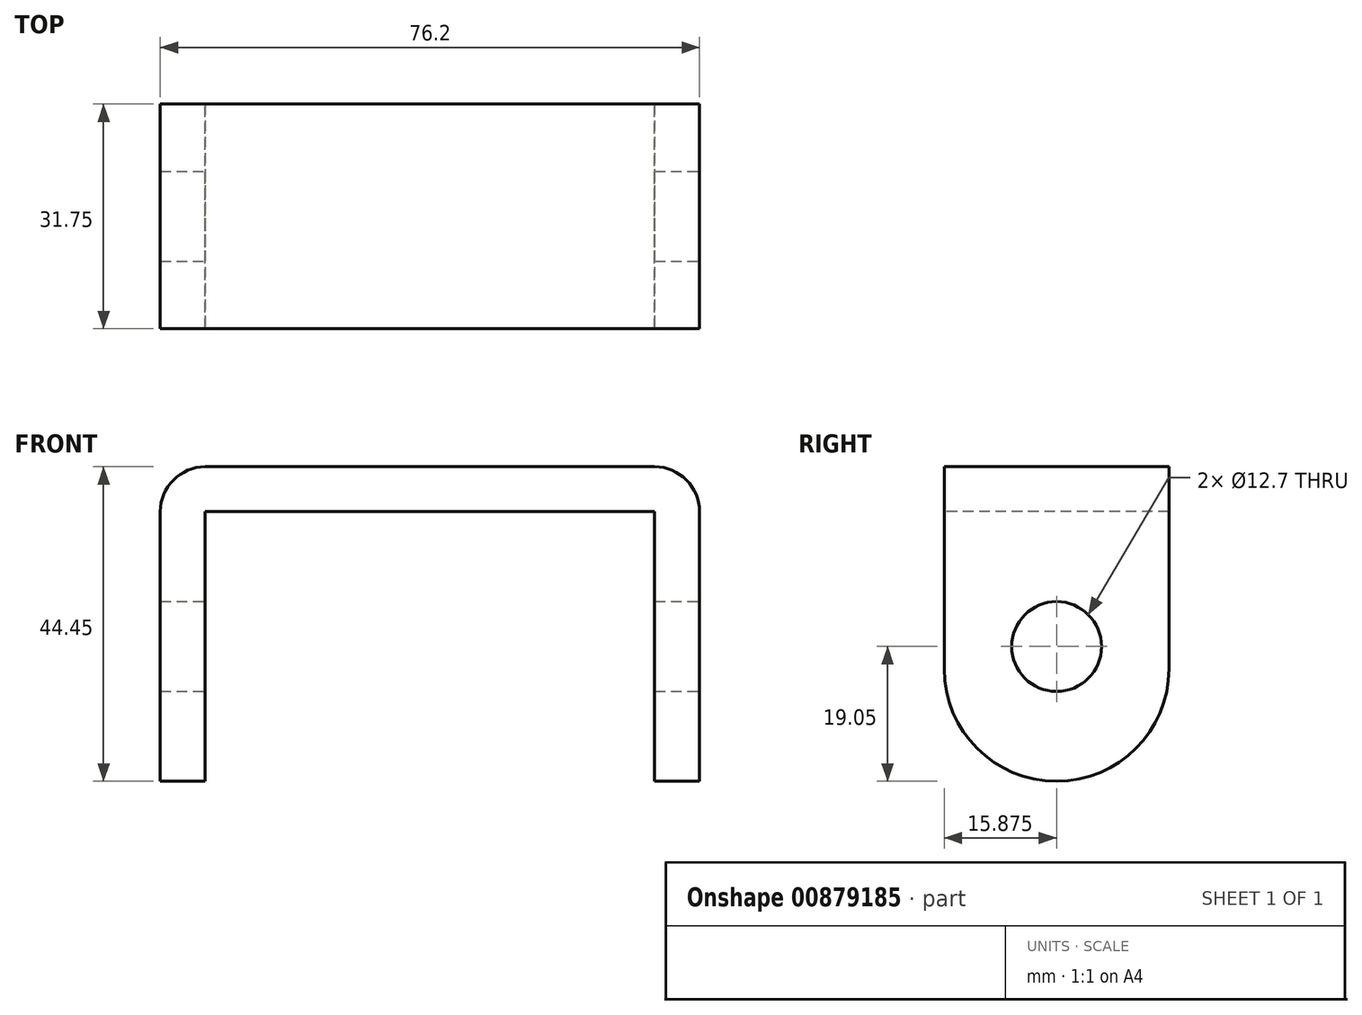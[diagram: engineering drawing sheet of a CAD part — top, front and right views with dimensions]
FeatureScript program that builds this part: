
annotation { "Feature Type Name" : "Feature", "Feature Type Description" : "" }
export const myFeature = defineFeature(function(context is Context, id is Id, definition is map)
    precondition{}
    {
        {
            var Q0;
            Q0=qCreatedBy(makeId("Front.planeOp"),FACE);
            var sketch = newSketch(context, id + "F0", { "sketchPlane" : qUnion([Q0])});
            skLineSegment(sketch, "E0.bottom", {"start": v(0, 0) * mm, "end": v(-76.2, 0) * mm});
            skLineSegment(sketch, "E0.top", {"start": v(0, 6.35) * mm, "end": v(-76.2, 6.35) * mm});
            skLineSegment(sketch, "E0.left", {"start": v(0, 0) * mm, "end": v(0, 6.35) * mm});
            skLineSegment(sketch, "E0.right", {"start": v(-76.2, 0) * mm, "end": v(-76.2, 6.35) * mm});
            skLineSegment(sketch, "E1.bottom", {"start": v(-76.2, 0) * mm, "end": v(-69.85, 0) * mm});
            skLineSegment(sketch, "E1.top", {"start": v(-76.2, -38.1) * mm, "end": v(-69.85, -38.1) * mm});
            skLineSegment(sketch, "E1.left", {"start": v(-76.2, 0) * mm, "end": v(-76.2, -38.1) * mm});
            skLineSegment(sketch, "E1.right", {"start": v(-69.85, 0) * mm, "end": v(-69.85, -38.1) * mm});
            skLineSegment(sketch, "E2.bottom", {"start": v(0, 0) * mm, "end": v(-6.35, 0) * mm});
            skLineSegment(sketch, "E2.top", {"start": v(0, -38.1) * mm, "end": v(-6.35, -38.1) * mm});
            skLineSegment(sketch, "E2.left", {"start": v(0, 0) * mm, "end": v(0, -38.1) * mm});
            skLineSegment(sketch, "E2.right", {"start": v(-6.35, 0) * mm, "end": v(-6.35, -38.1) * mm});
            skSolve(sketch);
        }
        {
            var Q0;
            Q0=qSketchRegion(id+"F0",true);
            extrude(context, id + "F1", {"entities" : qUnion([Q0]), "depth" : 31.75 * mm, "offsetDistance" : 25.4 * mm});
        }
        {
            var Q0;
            Q0=makeQuery(id+"F1.opExtrude","SWEPT_FACE",FACE,{"disambiguationData":[OSD([sQuery(id+"F0.wireOp",EDGE,"E0.left"),sQuery(id+"F0.wireOp",EDGE,"E2.left")])]});
            var sketch = newSketch(context, id + "F2", { "sketchPlane" : qUnion([Q0])});
            skCircle(sketch, "E3", {"center": v(-15.88, -19.05) * mm, "radius": 6.35 * mm});
            skSolve(sketch);
        }
        {
            var Q0;
            Q0=qSketchRegion(id+"F2",true);
            extrude(context, id + "F3", {"entities" : qUnion([Q0]), "operationType" : NewBodyOperationType.REMOVE, "oppositeDirection" : true, "depth" : 127 * mm, "offsetDistance" : 25.4 * mm});
        }
        {
            var Q0;
            Q0=makeQuery(id+"F1.opExtrude","SWEPT_FACE",FACE,{"disambiguationData":[OSD([sQuery(id+"F0.wireOp",EDGE,"E0.left"),sQuery(id+"F0.wireOp",EDGE,"E2.left")])]});
            var sketch = newSketch(context, id + "F4", { "sketchPlane" : qUnion([Q0])});
            skLineSegment(sketch, "E4.bottom", {"start": v(-15.88, -38.1) * mm, "end": v(-15.87, -38.1) * mm});
            skLineSegment(sketch, "E4.top", {"start": v(-31.75, 6.35) * mm, "end": v(0, 6.35) * mm});
            skLineSegment(sketch, "E4.left", {"start": v(-31.75, -22.23) * mm, "end": v(-31.75, 6.35) * mm});
            skLineSegment(sketch, "E4.right", {"start": v(0, -22.22) * mm, "end": v(0, 6.35) * mm});
            skPoint(sketch, "E5.visualSharp", {"position": v(-31.75, -38.1) * mm});
            skArc(sketch, "E5.filletArc", {"start": v(-31.75, -22.23) * mm, "mid": v(-27.1, -33.45) * mm, "end": v(-15.88, -38.1) * mm});
            skPoint(sketch, "E6.visualSharp", {"position": v(0, -38.1) * mm});
            skArc(sketch, "E6.filletArc", {"start": v(-15.87, -38.1) * mm, "mid": v(-4.65, -33.45) * mm, "end": v(0, -22.22) * mm});
            skSolve(sketch);
        }
        {
            var Q0;
            {var subQ0=sQuery(id+"F4.wireOp",EDGE,"E5.filletArc");Q0=makeQuery(id+"F4.imprint","IMPRINT",FACE,{"disambiguationData":[TD([[makeQuery(id+"F4.imprint","IMPRINT",EDGE,{"derivedFrom":subQ0}),-1.0]])]});}
            var Q1;
            {var subQ0=sQuery(id+"F4.wireOp",EDGE,"E6.filletArc");Q1=makeQuery(id+"F4.imprint","IMPRINT",FACE,{"disambiguationData":[TD([[makeQuery(id+"F4.imprint","IMPRINT",EDGE,{"derivedFrom":subQ0}),-1.0]])]});}
            extrude(context, id + "F5", {"entities" : qUnion([Q0, Q1]), "operationType" : NewBodyOperationType.REMOVE, "oppositeDirection" : true, "depth" : 127 * mm, "offsetDistance" : 25.4 * mm});
        }
        {
            var Q0;
            Q0=makeQuery(id+"F1.opExtrude","CAP_FACE",FACE,{"disambiguationData":[OSD([sQuery(id+"F0.wireOp",EDGE,"E0.bottom"),sQuery(id+"F0.wireOp",EDGE,"E0.top"),sQuery(id+"F0.wireOp",EDGE,"E0.left"),sQuery(id+"F0.wireOp",EDGE,"E0.right"),sQuery(id+"F0.wireOp",EDGE,"E1.top"),sQuery(id+"F0.wireOp",EDGE,"E1.left"),sQuery(id+"F0.wireOp",EDGE,"E1.right"),sQuery(id+"F0.wireOp",EDGE,"E2.top"),sQuery(id+"F0.wireOp",EDGE,"E2.left"),sQuery(id+"F0.wireOp",EDGE,"E2.right")])],"isStart":false});
            var sketch = newSketch(context, id + "F6", { "sketchPlane" : qUnion([Q0])});
            skLineSegment(sketch, "E7.bottom", {"start": v(-69.85, 6.35) * mm, "end": v(-6.35, 6.35) * mm});
            skLineSegment(sketch, "E7.top", {"start": v(-63.5, 0) * mm, "end": v(-12.7, 0) * mm});
            skLineSegment(sketch, "E7.left", {"start": v(-76.2, 0) * mm, "end": v(-76.2, 0) * mm});
            skLineSegment(sketch, "E7.right", {"start": v(0, 0) * mm, "end": v(0, 0) * mm});
            skLineSegment(sketch, "E8.bottom", {"start": v(0, 0) * mm, "end": v(-6.35, 0) * mm});
            skLineSegment(sketch, "E8.top", {"start": v(0, -22.23) * mm, "end": v(-6.35, -22.23) * mm});
            skLineSegment(sketch, "E8.left", {"start": v(0, 0) * mm, "end": v(0, -22.23) * mm});
            skLineSegment(sketch, "E8.right", {"start": v(-6.35, -6.35) * mm, "end": v(-6.35, -22.23) * mm});
            skLineSegment(sketch, "E9.bottom", {"start": v(-69.85, -22.23) * mm, "end": v(-76.2, -22.23) * mm});
            skLineSegment(sketch, "E9.top", {"start": v(-69.85, 0) * mm, "end": v(-76.2, 0) * mm});
            skLineSegment(sketch, "E9.left", {"start": v(-69.85, -22.23) * mm, "end": v(-69.85, -6.35) * mm});
            skLineSegment(sketch, "E9.right", {"start": v(-76.2, -22.23) * mm, "end": v(-76.2, 0) * mm});
            skPoint(sketch, "E10.visualSharp", {"position": v(-76.2, 6.35) * mm});
            skArc(sketch, "E10.filletArc", {"start": v(-69.85, 6.35) * mm, "mid": v(-74.34, 4.5) * mm, "end": v(-76.2, 0) * mm});
            skArc(sketch, "E11.filletArc", {"start": v(-63.5, 0) * mm, "mid": v(-68, -1.86) * mm, "end": v(-69.85, -6.35) * mm});
            skArc(sketch, "E12.filletArc", {"start": v(-6.35, -6.35) * mm, "mid": v(-8.2, -1.86) * mm, "end": v(-12.7, 0) * mm});
            skPoint(sketch, "E13.visualSharp", {"position": v(0, 6.35) * mm});
            skArc(sketch, "E13.filletArc", {"start": v(0, 0) * mm, "mid": v(-1.86, 4.5) * mm, "end": v(-6.35, 6.35) * mm});
            skSolve(sketch);
        }
        {
            var Q0;
            {var subQ0=sQuery(id+"F6.wireOp",EDGE,"E11.filletArc");Q0=makeQuery(id+"F6.imprint","IMPRINT",FACE,{"disambiguationData":[TD([[makeQuery(id+"F6.imprint","IMPRINT",EDGE,{"derivedFrom":subQ0}),-1.0]])]});}
            var Q1;
            {var subQ0=sQuery(id+"F6.wireOp",EDGE,"E12.filletArc");Q1=makeQuery(id+"F6.imprint","IMPRINT",FACE,{"disambiguationData":[TD([[makeQuery(id+"F6.imprint","IMPRINT",EDGE,{"derivedFrom":subQ0}),-1.0]])]});}
            extrude(context, id + "F7", {"entities" : qUnion([Q0, Q1]), "operationType" : NewBodyOperationType.ADD, "oppositeDirection" : true, "depth" : 31.75 * mm, "offsetDistance" : 25.4 * mm});
        }
        {
            var Q0;
            {var subQ0=sQuery(id+"F6.wireOp",EDGE,"E10.filletArc");Q0=makeQuery(id+"F6.imprint","IMPRINT",FACE,{"disambiguationData":[TD([[makeQuery(id+"F6.imprint","IMPRINT",EDGE,{"derivedFrom":subQ0}),-1.0]])]});}
            var Q1;
            {var subQ0=sQuery(id+"F6.wireOp",EDGE,"E13.filletArc");Q1=makeQuery(id+"F6.imprint","IMPRINT",FACE,{"disambiguationData":[TD([[makeQuery(id+"F6.imprint","IMPRINT",EDGE,{"derivedFrom":subQ0}),-1.0]])]});}
            var Q2;
            {var subQ0=sQuery(id+"F6.wireOp",EDGE,"E11.filletArc");Q2=makeQuery(id+"F6.imprint","IMPRINT",FACE,{"disambiguationData":[TD([[makeQuery(id+"F6.imprint","IMPRINT",EDGE,{"derivedFrom":subQ0}),-1.0]])]});}
            var Q3;
            {var subQ0=sQuery(id+"F6.wireOp",EDGE,"E12.filletArc");Q3=makeQuery(id+"F6.imprint","IMPRINT",FACE,{"disambiguationData":[TD([[makeQuery(id+"F6.imprint","IMPRINT",EDGE,{"derivedFrom":subQ0}),-1.0]])]});}
            extrude(context, id + "F8", {"entities" : qUnion([Q0, Q1, Q2, Q3]), "operationType" : NewBodyOperationType.REMOVE, "oppositeDirection" : true, "depth" : 31.75 * mm, "offsetDistance" : 25.4 * mm});
        }
    });
